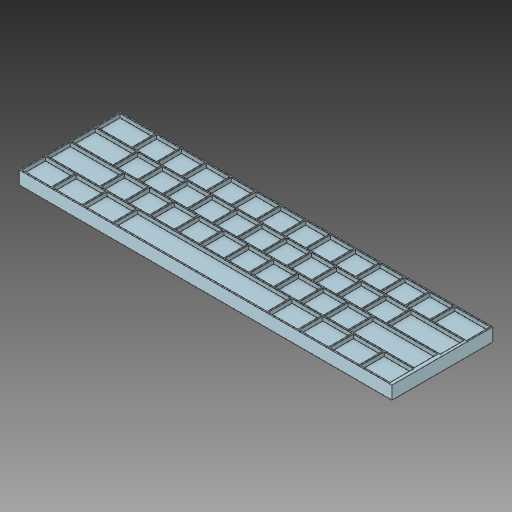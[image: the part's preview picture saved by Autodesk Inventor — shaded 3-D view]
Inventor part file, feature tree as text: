
AUTODESK INVENTOR PART (.ipt)
format: ipt  version: 2018 (Build 220112000, 112)  size: 450,048 bytes
history: native  units: mm
features: extrude x2, other x2, projected_geometry x1
ambient origin geometry x8: Origin, YZ Plane, XZ Plane, XY Plane, X Axis, Y Axis, Z Axis, Center Point
bodies: Solid1 (feature_tree)
feature tree (5):
  extrude  "Keyboard Backplane Body"  Depth=77.0mm
  extrude  "Keycap Holes"  Depth=285.0mm
  other  "Keyboard Backplane"
  other  "KeyCap Outlines"
  projected_geometry  "Projected Loop1"
